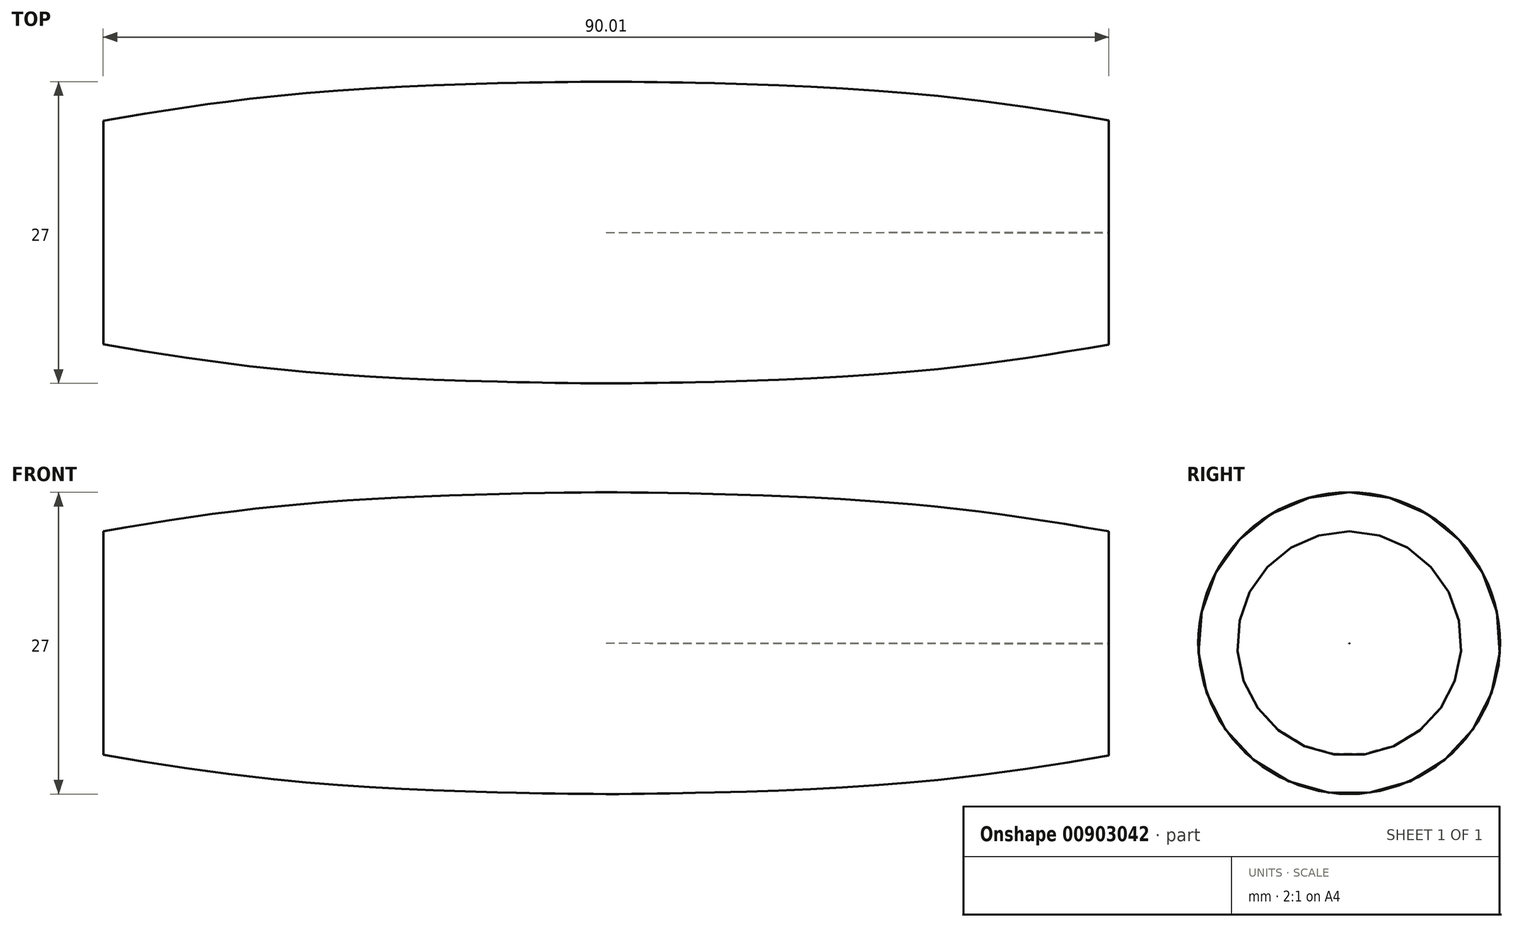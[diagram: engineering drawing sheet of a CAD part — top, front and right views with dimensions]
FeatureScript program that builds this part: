
annotation { "Feature Type Name" : "Feature", "Feature Type Description" : "" }
export const myFeature = defineFeature(function(context is Context, id is Id, definition is map)
    precondition{}
    {
        {
            var Q0;
            Q0=qCreatedBy(makeId("Front.planeOp"),FACE);
            var sketch = newSketch(context, id + "F0", { "sketchPlane" : qUnion([Q0])});
            skLineSegment(sketch, "E0", {"start": v(0, 0) * mm, "end": v(45, 0) * mm});
            skLineSegment(sketch, "E1", {"start": v(45, 0) * mm, "end": v(45, 10) * mm});
            skFitSpline(sketch, "E2", {"points": [v(0, 13.5) * mm, v(21.44, 12.87) * mm, v(45, 10) * mm], "startDerivative": vector(18.36, 0) * mm, "endDerivative": vector(46.67, -8.18) * mm});
            skLineSegment(sketch, "E3", {"start": v(45, 0) * mm, "end": v(0, 0) * mm});
            skLineSegment(sketch, "E4", {"start": v(0, 13.5) * mm, "end": v(0, 0) * mm});
            skFitSpline(sketch, "E5.MirrorCS", {"points": [v(0, 13.5) * mm, v(-21.43, 12.88) * mm, v(-45, 10.02) * mm], "startDerivative": vector(-18.36, 0) * mm, "endDerivative": vector(-46.67, -8.16) * mm});
            skLineSegment(sketch, "E6.MirrorCS", {"start": v(-45, 0.02) * mm, "end": v(-45, 10.02) * mm});
            skLineSegment(sketch, "E7.MirrorCS", {"start": v(-45, 0.02) * mm, "end": v(0, 0) * mm});
            skSolve(sketch);
        }
        {
            var Q0;
            Q0 = qSketchRegion(id + "F0", true);
            var Q1;
            Q1=sQuery(id+"F0.wireOp",EDGE,"E7.MirrorCS");
            revolve(context, id + "F1", {"surfaceOperationType" : NewSurfaceOperationType.NEW, "entities" : qUnion([Q0]), "axis" : qUnion([Q1]), "revolveType" : RevolveType.FULL});
        }
    });
